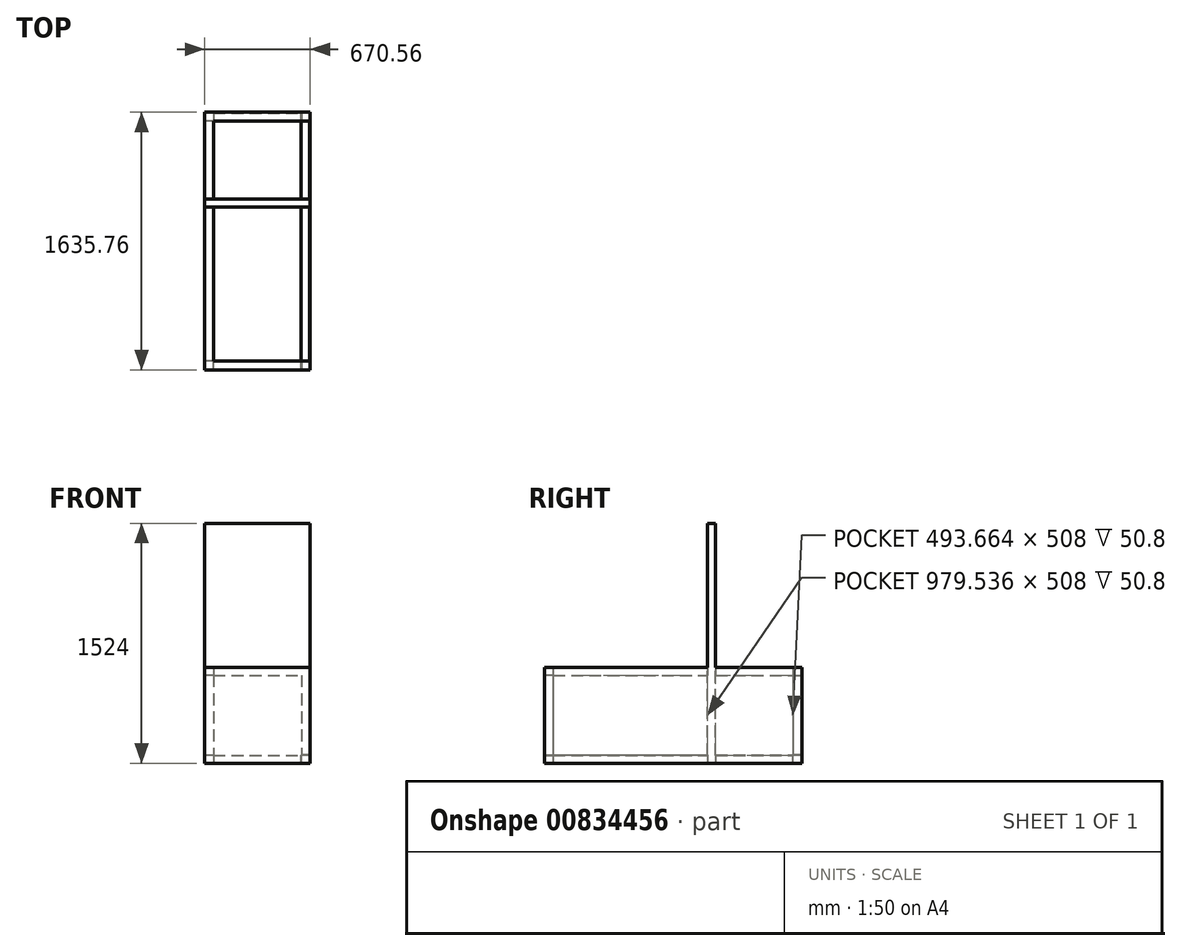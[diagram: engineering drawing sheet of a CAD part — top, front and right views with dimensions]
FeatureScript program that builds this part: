
annotation { "Feature Type Name" : "Feature", "Feature Type Description" : "" }
export const myFeature = defineFeature(function(context is Context, id is Id, definition is map)
    precondition{}
    {
        {
            var Q0;
            Q0=qCreatedBy(makeId("Top.planeOp"),FACE);
            var sketch = newSketch(context, id + "F0", { "sketchPlane" : qUnion([Q0])});
            skLineSegment(sketch, "E0.bottom", {"start": v(-609.6, -762) * mm, "end": v(609.6, -762) * mm});
            skLineSegment(sketch, "E0.top", {"start": v(-609.6, 762) * mm, "end": v(609.6, 762) * mm});
            skLineSegment(sketch, "E0.left", {"start": v(-609.6, -762) * mm, "end": v(-609.6, 762) * mm});
            skLineSegment(sketch, "E0.right", {"start": v(609.6, -762) * mm, "end": v(609.6, 762) * mm});
            skPoint(sketch, "E0.middle", {"position": v(0, 0) * mm});
            skLineSegment(sketch, "E1.0", {"start": v(660.4, -812.8) * mm, "end": v(660.4, 812.8) * mm});
            skLineSegment(sketch, "E1.1", {"start": v(-660.4, -812.8) * mm, "end": v(660.4, -812.8) * mm});
            skLineSegment(sketch, "E1.2", {"start": v(-660.4, -812.8) * mm, "end": v(-660.4, 812.8) * mm});
            skLineSegment(sketch, "E1.3", {"start": v(-660.4, 812.8) * mm, "end": v(660.4, 812.8) * mm});
            skSolve(sketch);
        }
        {
            var Q0;
            Q0=makeQuery(id+"F0.imprint","IMPRINT",FACE,{"disambiguationData":[TD([[makeQuery(id+"F0.imprint","IMPRINT",EDGE,{"derivedFrom":sQuery(id+"F0.wireOp",EDGE,"E0.bottom")}),-1.0]])]});
            extrude(context, id + "F1", {"entities" : qUnion([Q0]), "depth" : 50.8 * mm, "offsetDistance" : 25.4 * mm});
        }
        {
            var Q0;
            Q0=makeQuery(id+"F1.opExtrude","CAP_FACE",FACE,{"disambiguationData":[OSD([sQuery(id+"F0.wireOp",EDGE,"E0.bottom"),sQuery(id+"F0.wireOp",EDGE,"E0.top"),sQuery(id+"F0.wireOp",EDGE,"E0.left"),sQuery(id+"F0.wireOp",EDGE,"E0.right"),sQuery(id+"F0.wireOp",EDGE,"E1.0"),sQuery(id+"F0.wireOp",EDGE,"E1.1"),sQuery(id+"F0.wireOp",EDGE,"E1.2"),sQuery(id+"F0.wireOp",EDGE,"E1.3")])],"isStart":false});
            var sketch = newSketch(context, id + "F2", { "sketchPlane" : qUnion([Q0])});
            skLineSegment(sketch, "E2", {"start": v(-660.4, 812.8) * mm, "end": v(-609.6, 812.8) * mm});
            skLineSegment(sketch, "E3", {"start": v(-609.6, 812.8) * mm, "end": v(-609.6, 762) * mm});
            skLineSegment(sketch, "E4", {"start": v(-609.6, 762) * mm, "end": v(-660.4, 762) * mm});
            skLineSegment(sketch, "E5", {"start": v(-660.4, 762) * mm, "end": v(-660.4, 812.8) * mm});
            skLineSegment(sketch, "E6.MirrorCS", {"start": v(660.4, 812.8) * mm, "end": v(609.6, 812.8) * mm});
            skLineSegment(sketch, "E7.MirrorCS", {"start": v(609.6, 812.8) * mm, "end": v(609.6, 762) * mm});
            skLineSegment(sketch, "E8.MirrorCS", {"start": v(660.4, 762) * mm, "end": v(660.4, 812.8) * mm});
            skLineSegment(sketch, "E9.MirrorCS", {"start": v(609.6, 762) * mm, "end": v(660.4, 762) * mm});
            skLineSegment(sketch, "E10.MirrorCS", {"start": v(609.6, -762) * mm, "end": v(660.4, -762) * mm});
            skLineSegment(sketch, "E11.MirrorCS", {"start": v(-660.4, -812.8) * mm, "end": v(-609.6, -812.8) * mm});
            skLineSegment(sketch, "E12.MirrorCS", {"start": v(-609.6, -812.8) * mm, "end": v(-609.6, -762) * mm});
            skLineSegment(sketch, "E13.MirrorCS", {"start": v(660.4, -762) * mm, "end": v(660.4, -812.8) * mm});
            skLineSegment(sketch, "E14.MirrorCS", {"start": v(-609.6, -762) * mm, "end": v(-660.4, -762) * mm});
            skLineSegment(sketch, "E15.MirrorCS", {"start": v(609.6, -812.8) * mm, "end": v(609.6, -762) * mm});
            skLineSegment(sketch, "E16.MirrorCS", {"start": v(660.4, -812.8) * mm, "end": v(609.6, -812.8) * mm});
            skLineSegment(sketch, "E17.MirrorCS", {"start": v(-660.4, -762) * mm, "end": v(-660.4, -812.8) * mm});
            skSolve(sketch);
        }
        {
            var Q0;
            Q0=qSketchRegion(id+"F2",true);
            extrude(context, id + "F3", {"entities" : qUnion([Q0]), "operationType" : NewBodyOperationType.ADD, "depth" : 508 * mm, "offsetDistance" : 25.4 * mm});
        }
        {
            var Q0;
            Q0=makeQuery(id+"F3.opExtrude","CAP_FACE",FACE,{"disambiguationData":[OSD([sQuery(id+"F2.wireOp",EDGE,"E2"),sQuery(id+"F2.wireOp",EDGE,"E3"),sQuery(id+"F2.wireOp",EDGE,"E4"),sQuery(id+"F2.wireOp",EDGE,"E5")])],"isStart":false});
            var sketch = newSketch(context, id + "F4", { "sketchPlane" : qUnion([Q0])});
            skLineSegment(sketch, "E18.bottom", {"start": v(-609.6, -762) * mm, "end": v(609.6, -762) * mm});
            skLineSegment(sketch, "E18.top", {"start": v(-609.6, 762) * mm, "end": v(609.6, 762) * mm});
            skLineSegment(sketch, "E18.left", {"start": v(-609.6, -762) * mm, "end": v(-609.6, 762) * mm});
            skLineSegment(sketch, "E18.right", {"start": v(609.6, -762) * mm, "end": v(609.6, 762) * mm});
            skPoint(sketch, "E18.middle", {"position": v(0, 0) * mm});
            skLineSegment(sketch, "E19.0", {"start": v(-660.4, -812.8) * mm, "end": v(660.4, -812.8) * mm});
            skLineSegment(sketch, "E19.1", {"start": v(-660.4, -812.8) * mm, "end": v(-660.4, 812.8) * mm});
            skLineSegment(sketch, "E19.2", {"start": v(-660.4, 812.8) * mm, "end": v(660.4, 812.8) * mm});
            skLineSegment(sketch, "E19.3", {"start": v(660.4, -812.8) * mm, "end": v(660.4, 812.8) * mm});
            skSolve(sketch);
        }
        {
            var Q0;
            Q0=qSketchRegion(id+"F4",true);
            extrude(context, id + "F5", {"entities" : qUnion([Q0]), "operationType" : NewBodyOperationType.ADD, "depth" : 50.8 * mm, "offsetDistance" : 25.4 * mm});
        }
        {
            var Q0;
            Q0=makeQuery(id+"F5.opExtrude","SWEPT_FACE",FACE,{"disambiguationData":[OSD([sQuery(id+"F4.wireOp",EDGE,"E18.top")])]});
            var sketch = newSketch(context, id + "F6", { "sketchPlane" : qUnion([Q0])});
            skLineSegment(sketch, "E20", {"start": v(-609.6, 558.8) * mm, "end": v(-609.6, 609.6) * mm});
            skLineSegment(sketch, "E21", {"start": v(-609.6, 609.6) * mm, "end": v(0, 609.6) * mm});
            skLineSegment(sketch, "E22", {"start": v(0, 609.6) * mm, "end": v(0, 558.8) * mm});
            skLineSegment(sketch, "E23", {"start": v(0, 558.8) * mm, "end": v(-609.6, 558.8) * mm});
            skSolve(sketch);
        }
        {
            var Q0;
            Q0=makeQuery(id+"FCSgfiYEbyqsPuG_1.boolean.opBoolean","MERGE",FACE,{"derivedFrom":[makeQuery(id+"F5.opExtrude","CAP_FACE",FACE,{"disambiguationData":[OSD([sQuery(id+"F4.wireOp",EDGE,"E18.bottom"),sQuery(id+"F4.wireOp",EDGE,"E18.top"),sQuery(id+"F4.wireOp",EDGE,"E18.left"),sQuery(id+"F4.wireOp",EDGE,"E18.right"),sQuery(id+"F4.wireOp",EDGE,"E19.0"),sQuery(id+"F4.wireOp",EDGE,"E19.1"),sQuery(id+"F4.wireOp",EDGE,"E19.2"),sQuery(id+"F4.wireOp",EDGE,"E19.3")])],"isStart":false}),makeQuery(id+"FCSgfiYEbyqsPuG_1.opExtrude","SWEPT_FACE",FACE,{"disambiguationData":[OSD([sQuery(id+"F6.wireOp",EDGE,"E21")])]})]});
            var sketch = newSketch(context, id + "F7", { "sketchPlane" : qUnion([Q0])});
            skLineSegment(sketch, "E24", {"start": v(0, 762) * mm, "end": v(0, 812.8) * mm});
            skLineSegment(sketch, "E25", {"start": v(0, 812.8) * mm, "end": v(660.4, 812.8) * mm});
            skLineSegment(sketch, "E26", {"start": v(660.4, 812.8) * mm, "end": v(660.4, -812.8) * mm});
            skLineSegment(sketch, "E27", {"start": v(660.4, -812.8) * mm, "end": v(0, -812.8) * mm});
            skLineSegment(sketch, "E28", {"start": v(0, -812.8) * mm, "end": v(0, 762) * mm});
            skSolve(sketch);
        }
        {
            var Q0;
            Q0=qSketchRegion(id+"F7",true);
            extrude(context, id + "F8", {"entities" : qUnion([Q0]), "operationType" : NewBodyOperationType.REMOVE, "endBound" : BoundingType.THROUGH_ALL, "oppositeDirection" : true, "depth" : 25.4 * mm, "offsetDistance" : 25.4 * mm});
        }
        {
            var Q0;
            {var subQ0=sQuery(id+"F0.wireOp",EDGE,"E0.left");var subQ1=sQuery(id+"F0.wireOp",EDGE,"E1.3");var subQ2=sQuery(id+"F0.wireOp",EDGE,"E0.right");var subQ3=sQuery(id+"F0.wireOp",EDGE,"E0.top");var subQ4=makeQuery(id+"F1.opExtrude","CAP_FACE",FACE,{"disambiguationData":[OSD([sQuery(id+"F0.wireOp",EDGE,"E0.bottom"),subQ3,subQ0,subQ2,sQuery(id+"F0.wireOp",EDGE,"E1.0"),sQuery(id+"F0.wireOp",EDGE,"E1.1"),sQuery(id+"F0.wireOp",EDGE,"E1.2"),subQ1])],"isStart":false});Q0=makeQuery(id+"F3.boolean.opBoolean","SPLIT",FACE,{"disambiguationData":[TD([makeQuery(id+"F1.opExtrude","SWEPT_FACE",FACE,{"disambiguationData":[OSD([subQ1])]})])],"derivedFrom":subQ4});}
            var sketch = newSketch(context, id + "F9", { "sketchPlane" : qUnion([Q0])});
            skLineSegment(sketch, "E29", {"start": v(0, 812.8) * mm, "end": v(0, 762) * mm});
            skLineSegment(sketch, "E30", {"start": v(0, 762) * mm, "end": v(-50.8, 762) * mm});
            skLineSegment(sketch, "E31", {"start": v(-50.8, 762) * mm, "end": v(-50.8, 812.8) * mm});
            skLineSegment(sketch, "E32", {"start": v(-50.8, 812.8) * mm, "end": v(0, 812.8) * mm});
            skLineSegment(sketch, "E33.MirrorCS", {"start": v(-50.8, -812.8) * mm, "end": v(0, -812.8) * mm});
            skLineSegment(sketch, "E34.MirrorCS", {"start": v(0, -812.8) * mm, "end": v(0, -762) * mm});
            skLineSegment(sketch, "E35.MirrorCS", {"start": v(0, -762) * mm, "end": v(-50.8, -762) * mm});
            skLineSegment(sketch, "E36.MirrorCS", {"start": v(-50.8, -762) * mm, "end": v(-50.8, -812.8) * mm});
            skSolve(sketch);
        }
        {
            var Q0;
            Q0=qSketchRegion(id+"F9",true);
            extrude(context, id + "F10", {"entities" : qUnion([Q0]), "operationType" : NewBodyOperationType.ADD, "endBound" : BoundingType.UP_TO_NEXT, "depth" : 25.4 * mm, "offsetDistance" : 25.4 * mm});
        }
        {
            var Q0;
            {var subQ1=sQuery(id+"F0.wireOp",EDGE,"E0.top");var subQ7=sQuery(id+"F0.wireOp",EDGE,"E0.bottom");var subQ10=makeQuery(id+"F8.opExtrude","SWEPT_FACE",FACE,{"disambiguationData":[OSD([sQuery(id+"F7.wireOp",EDGE,"E24"),sQuery(id+"F7.wireOp",EDGE,"E28")])]});Q0=makeQuery(id+"FI0uP4kL5XJLF2I_1.boolean.opBoolean","MERGE",FACE,{"derivedFrom":[makeQuery(id+"F10.boolean.opBoolean","MERGE",FACE,{"derivedFrom":[makeQuery(id+"F8.boolean.opBoolean","MERGE",FACE,{"derivedFrom":[makeQuery(id+"FCSgfiYEbyqsPuG_1.opExtrude","SWEPT_FACE",FACE,{"disambiguationData":[OSD([sQuery(id+"F6.wireOp",EDGE,"E22")])]}),subQ10]}),makeQuery(id+"F8.boolean.opBoolean","COPY",FACE,{"disambiguationData":[TD([makeQuery(id+"F1.opExtrude","SWEPT_FACE",FACE,{"disambiguationData":[OSD([subQ7])]})])],"derivedFrom":subQ10}),makeQuery(id+"F8.boolean.opBoolean","COPY",FACE,{"disambiguationData":[TD([makeQuery(id+"F1.opExtrude","SWEPT_FACE",FACE,{"disambiguationData":[OSD([subQ1])]})])],"derivedFrom":subQ10}),makeQuery(id+"F10.opExtrude","SWEPT_FACE",FACE,{"disambiguationData":[OSD([sQuery(id+"F9.wireOp",EDGE,"E29")])]}),makeQuery(id+"F10.opExtrude","SWEPT_FACE",FACE,{"disambiguationData":[OSD([sQuery(id+"F9.wireOp",EDGE,"E34.MirrorCS")])]})]}),makeQuery(id+"FI0uP4kL5XJLF2I_1.opExtrude","SWEPT_FACE",FACE,{"disambiguationData":[OSD([sQuery(id+"FPcTlZiTrbIZ70A_1.wireOp",EDGE,"L0GQmyvb-ReXV-Bmec-5JdH-0vrgJq4hWDGI")])]})]});}
            var sketch = newSketch(context, id + "F11", { "sketchPlane" : qUnion([Q0])});
            skLineSegment(sketch, "E37", {"start": v(812.8, 0) * mm, "end": v(254, 0) * mm});
            skLineSegment(sketch, "E38", {"start": v(254, 0) * mm, "end": v(254, 254) * mm});
            skLineSegment(sketch, "E39", {"start": v(254, 254) * mm, "end": v(812.8, 254) * mm});
            skLineSegment(sketch, "E40", {"start": v(812.8, 254) * mm, "end": v(812.8, 0) * mm});
            skSolve(sketch);
        }
        {
            var Q0;
            Q0=qSketchRegion(id+"F11",true);
            extrude(context, id + "F12", {"entities" : qUnion([Q0]), "operationType" : NewBodyOperationType.ADD, "depth" : 558.8 * mm, "offsetDistance" : 25.4 * mm});
        }
        {
            var Q0;
            {var subQ0=sQuery(id+"F11.wireOp",EDGE,"E38");Q0=makeQuery(id+"Fa8mDGQ4B8yroh9_1.boolean.opBoolean","MERGE",FACE,{"derivedFrom":[makeQuery(id+"F12.opExtrude","SWEPT_FACE",FACE,{"disambiguationData":[OSD([subQ0])]}),makeQuery(id+"Fa8mDGQ4B8yroh9_1.opExtrude","SWEPT_FACE",FACE,{"disambiguationData":[OSD([subQ0])]})]});}
            var sketch = newSketch(context, id + "F13", { "sketchPlane" : qUnion([Q0])});
            skLineSegment(sketch, "E41.0", {"start": v(-0.63, 203.2) * mm, "end": v(508, 203.2) * mm});
            skLineSegment(sketch, "E41.1", {"start": v(-0.63, 50.8) * mm, "end": v(-0.63, 203.2) * mm});
            skLineSegment(sketch, "E41.2", {"start": v(508, 50.8) * mm, "end": v(-0.63, 50.8) * mm});
            skLineSegment(sketch, "E41.3", {"start": v(508, 203.2) * mm, "end": v(508, 50.8) * mm});
            skSolve(sketch);
        }
        {
            var Q0;
            Q0=makeQuery(id+"FCSgfiYEbyqsPuG_1.boolean.opBoolean","MERGE",FACE,{"derivedFrom":[makeQuery(id+"F5.opExtrude","CAP_FACE",FACE,{"disambiguationData":[OSD([sQuery(id+"F4.wireOp",EDGE,"E18.bottom"),sQuery(id+"F4.wireOp",EDGE,"E18.top"),sQuery(id+"F4.wireOp",EDGE,"E18.left"),sQuery(id+"F4.wireOp",EDGE,"E18.right"),sQuery(id+"F4.wireOp",EDGE,"E19.0"),sQuery(id+"F4.wireOp",EDGE,"E19.1"),sQuery(id+"F4.wireOp",EDGE,"E19.2"),sQuery(id+"F4.wireOp",EDGE,"E19.3")])],"isStart":false}),makeQuery(id+"FCSgfiYEbyqsPuG_1.opExtrude","SWEPT_FACE",FACE,{"disambiguationData":[OSD([sQuery(id+"F6.wireOp",EDGE,"E21")])]})]});
            var sketch = newSketch(context, id + "F14", { "sketchPlane" : qUnion([Q0])});
            skLineSegment(sketch, "E42.0", {"start": v(-635, -787.4) * mm, "end": v(-635, 787.4) * mm});
            skLineSegment(sketch, "E42.1", {"start": v(-635, -787.4) * mm, "end": v(-25.4, -787.4) * mm});
            skLineSegment(sketch, "E42.2", {"start": v(-25.4, -787.4) * mm, "end": v(-25.4, 787.4) * mm});
            skLineSegment(sketch, "E42.3", {"start": v(-635, 787.4) * mm, "end": v(-25.4, 787.4) * mm});
            skSolve(sketch);
        }
        {
            var Q0;
            Q0=makeQuery(id+"F12.boolean.opBoolean","MERGE",FACE,{"derivedFrom":[makeQuery(id+"FI0uP4kL5XJLF2I_1.boolean.opBoolean","MERGE",FACE,{"derivedFrom":[makeQuery(id+"F1.opExtrude","CAP_FACE",FACE,{"disambiguationData":[OSD([sQuery(id+"F0.wireOp",EDGE,"E0.bottom"),sQuery(id+"F0.wireOp",EDGE,"E0.top"),sQuery(id+"F0.wireOp",EDGE,"E0.left"),sQuery(id+"F0.wireOp",EDGE,"E0.right"),sQuery(id+"F0.wireOp",EDGE,"E1.0"),sQuery(id+"F0.wireOp",EDGE,"E1.1"),sQuery(id+"F0.wireOp",EDGE,"E1.2"),sQuery(id+"F0.wireOp",EDGE,"E1.3")])],"isStart":true}),makeQuery(id+"FI0uP4kL5XJLF2I_1.opExtrude","SWEPT_FACE",FACE,{"disambiguationData":[OSD([sQuery(id+"FPcTlZiTrbIZ70A_1.wireOp",EDGE,"5B50FkJB-d4VW-NrSr-TGA2-GngbR9WeU5De")])]})]}),makeQuery(id+"F12.opExtrude","SWEPT_FACE",FACE,{"disambiguationData":[OSD([sQuery(id+"F11.wireOp",EDGE,"E37")])]})]});
            var sketch = newSketch(context, id + "F15", { "sketchPlane" : qUnion([Q0])});
            skSolve(sketch);
        }
        {
            var Q0;
            {var subQ0=sQuery(id+"F11.wireOp",EDGE,"E39");Q0=makeQuery(id+"Fa8mDGQ4B8yroh9_1.boolean.opBoolean","MERGE",FACE,{"derivedFrom":[makeQuery(id+"F12.opExtrude","SWEPT_FACE",FACE,{"disambiguationData":[OSD([subQ0])]}),makeQuery(id+"Fa8mDGQ4B8yroh9_1.opExtrude","SWEPT_FACE",FACE,{"disambiguationData":[OSD([subQ0])]})]});}
            var sketch = newSketch(context, id + "F16", { "sketchPlane" : qUnion([Q0])});
            skPoint(sketch, "E43", {"position": v(279.4, 533.4) * mm});
            skCircle(sketch, "E44", {"center": v(279.4, 533.4) * mm, "radius": 228.6 * mm});
            skSolve(sketch);
        }
        {
            var Q0;
            Q0=makeQuery(id+"F12.boolean.opBoolean","MERGE",FACE,{"derivedFrom":[makeQuery(id+"F10.boolean.opBoolean","MERGE",FACE,{"derivedFrom":[makeQuery(id+"F5.boolean.opBoolean","MERGE",FACE,{"derivedFrom":[makeQuery(id+"F3.boolean.opBoolean","MERGE",FACE,{"derivedFrom":[makeQuery(id+"F1.opExtrude","SWEPT_FACE",FACE,{"disambiguationData":[OSD([sQuery(id+"F0.wireOp",EDGE,"E1.3")])]}),makeQuery(id+"F3.opExtrude","SWEPT_FACE",FACE,{"disambiguationData":[OSD([sQuery(id+"F2.wireOp",EDGE,"E2")])]}),makeQuery(id+"F3.opExtrude","SWEPT_FACE",FACE,{"disambiguationData":[OSD([sQuery(id+"F2.wireOp",EDGE,"E6.MirrorCS")])]})]}),makeQuery(id+"F5.opExtrude","SWEPT_FACE",FACE,{"disambiguationData":[OSD([sQuery(id+"F4.wireOp",EDGE,"E19.2")])]})]}),makeQuery(id+"F10.opExtrude","SWEPT_FACE",FACE,{"disambiguationData":[OSD([sQuery(id+"F9.wireOp",EDGE,"E32")])]})]}),makeQuery(id+"F12.opExtrude","SWEPT_FACE",FACE,{"disambiguationData":[OSD([sQuery(id+"F11.wireOp",EDGE,"E40")])]})]});
            var sketch = newSketch(context, id + "F17", { "sketchPlane" : qUnion([Q0])});
            skLineSegment(sketch, "E45.bottom", {"start": v(0, 254) * mm, "end": v(-558.8, 254) * mm});
            skLineSegment(sketch, "E45.top", {"start": v(0, 0) * mm, "end": v(-558.8, 0) * mm});
            skLineSegment(sketch, "E45.left", {"start": v(0, 254) * mm, "end": v(0, 0) * mm});
            skLineSegment(sketch, "E45.right", {"start": v(-558.8, 254) * mm, "end": v(-558.8, 0) * mm});
            skSolve(sketch);
        }
        {
            var Q0;
            Q0=qSketchRegion(id+"F17",true);
            extrude(context, id + "F18", {"entities" : qUnion([Q0]), "operationType" : NewBodyOperationType.REMOVE, "endBound" : BoundingType.THROUGH_ALL, "oppositeDirection" : true, "depth" : 25.4 * mm, "offsetDistance" : 25.4 * mm});
        }
        {
            var Q0;
            {var subQ1=sQuery(id+"F0.wireOp",EDGE,"E0.top");var subQ7=sQuery(id+"F0.wireOp",EDGE,"E0.bottom");var subQ10=makeQuery(id+"F8.opExtrude","SWEPT_FACE",FACE,{"disambiguationData":[OSD([sQuery(id+"F7.wireOp",EDGE,"E24"),sQuery(id+"F7.wireOp",EDGE,"E28")])]});Q0=makeQuery(id+"F18.boolean.opBoolean","MERGE",FACE,{"derivedFrom":[makeQuery(id+"F10.boolean.opBoolean","MERGE",FACE,{"derivedFrom":[makeQuery(id+"F8.boolean.opBoolean","MERGE",FACE,{"derivedFrom":[makeQuery(id+"FCSgfiYEbyqsPuG_1.opExtrude","SWEPT_FACE",FACE,{"disambiguationData":[OSD([sQuery(id+"F6.wireOp",EDGE,"E22")])]}),subQ10]}),makeQuery(id+"F8.boolean.opBoolean","COPY",FACE,{"disambiguationData":[TD([makeQuery(id+"F1.opExtrude","SWEPT_FACE",FACE,{"disambiguationData":[OSD([subQ7])]})])],"derivedFrom":subQ10}),makeQuery(id+"F8.boolean.opBoolean","COPY",FACE,{"disambiguationData":[TD([makeQuery(id+"F1.opExtrude","SWEPT_FACE",FACE,{"disambiguationData":[OSD([subQ1])]})])],"derivedFrom":subQ10}),makeQuery(id+"F10.opExtrude","SWEPT_FACE",FACE,{"disambiguationData":[OSD([sQuery(id+"F9.wireOp",EDGE,"E29")])]}),makeQuery(id+"F10.opExtrude","SWEPT_FACE",FACE,{"disambiguationData":[OSD([sQuery(id+"F9.wireOp",EDGE,"E34.MirrorCS")])]})]}),makeQuery(id+"F18.opExtrude","SWEPT_FACE",FACE,{"disambiguationData":[OSD([sQuery(id+"F17.wireOp",EDGE,"E45.left")])]})]});}
            var sketch = newSketch(context, id + "F19", { "sketchPlane" : qUnion([Q0])});
            skLineSegment(sketch, "E46.bottom", {"start": v(-812.8, 609.6) * mm, "end": v(812.8, 609.6) * mm});
            skLineSegment(sketch, "E46.top", {"start": v(-812.8, 0) * mm, "end": v(812.8, 0) * mm});
            skLineSegment(sketch, "E46.left", {"start": v(-812.8, 609.6) * mm, "end": v(-812.8, 0) * mm});
            skLineSegment(sketch, "E46.right", {"start": v(812.8, 609.6) * mm, "end": v(812.8, 0) * mm});
            skSolve(sketch);
        }
        {
            var Q0;
            Q0=qSketchRegion(id+"F19",true);
            extrude(context, id + "F20", {"entities" : qUnion([Q0]), "operationType" : NewBodyOperationType.ADD, "surfaceOperationType" : NewSurfaceOperationType.ADD, "depth" : 5.08 * mm, "offsetDistance" : 25.4 * mm});
        }
        {
            var Q0;
            Q0=makeQuery(id+"F5.boolean.opBoolean","MERGE",FACE,{"derivedFrom":[makeQuery(id+"F3.boolean.opBoolean","MERGE",FACE,{"derivedFrom":[makeQuery(id+"F1.opExtrude","SWEPT_FACE",FACE,{"disambiguationData":[OSD([sQuery(id+"F0.wireOp",EDGE,"E1.2")])]}),makeQuery(id+"F3.opExtrude","SWEPT_FACE",FACE,{"disambiguationData":[OSD([sQuery(id+"F2.wireOp",EDGE,"E5")])]}),makeQuery(id+"F3.opExtrude","SWEPT_FACE",FACE,{"disambiguationData":[OSD([sQuery(id+"F2.wireOp",EDGE,"E17.MirrorCS")])]})]}),makeQuery(id+"F5.opExtrude","SWEPT_FACE",FACE,{"disambiguationData":[OSD([sQuery(id+"F4.wireOp",EDGE,"E19.1")])]})]});
            var sketch = newSketch(context, id + "F21", { "sketchPlane" : qUnion([Q0])});
            skLineSegment(sketch, "E47.bottom", {"start": v(-812.8, 609.6) * mm, "end": v(812.8, 609.6) * mm});
            skLineSegment(sketch, "E47.top", {"start": v(-812.8, 0) * mm, "end": v(812.8, 0) * mm});
            skLineSegment(sketch, "E47.left", {"start": v(-812.8, 609.6) * mm, "end": v(-812.8, 0) * mm});
            skLineSegment(sketch, "E47.right", {"start": v(812.8, 609.6) * mm, "end": v(812.8, 0) * mm});
            skSolve(sketch);
        }
        {
            var Q0;
            Q0=qSketchRegion(id+"F21",true);
            extrude(context, id + "F22", {"entities" : qUnion([Q0]), "operationType" : NewBodyOperationType.ADD, "depth" : 5.08 * mm, "offsetDistance" : 25.4 * mm});
        }
        {
            var Q0;
            Q0=makeQuery(id+"F20.opExtrude","CAP_FACE",FACE,{"disambiguationData":[OSD([sQuery(id+"F19.wireOp",EDGE,"E46.bottom"),sQuery(id+"F19.wireOp",EDGE,"E46.top"),sQuery(id+"F19.wireOp",EDGE,"E46.left"),sQuery(id+"F19.wireOp",EDGE,"E46.right")])],"isStart":true});
            var sketch = newSketch(context, id + "F23", { "sketchPlane" : qUnion([Q0])});
            skLineSegment(sketch, "E48.bottom", {"start": v(811.74, 0) * mm, "end": v(-815.7, 0) * mm});
            skLineSegment(sketch, "E48.top", {"start": v(811.74, 51.7) * mm, "end": v(-815.7, 51.7) * mm});
            skLineSegment(sketch, "E48.left", {"start": v(811.74, 0) * mm, "end": v(811.74, 51.7) * mm});
            skLineSegment(sketch, "E48.right", {"start": v(-815.7, 0) * mm, "end": v(-815.7, 51.7) * mm});
            skSolve(sketch);
        }
        {
            var Q0;
            Q0=qSketchRegion(id+"F23",true);
            extrude(context, id + "F24", {"entities" : qUnion([Q0]), "operationType" : NewBodyOperationType.ADD, "depth" : 53.34 * mm, "offsetDistance" : 25.4 * mm});
        }
        {
            var Q0;
            Q0=makeQuery(id+"F20.opExtrude","CAP_FACE",FACE,{"disambiguationData":[OSD([sQuery(id+"F19.wireOp",EDGE,"E46.bottom"),sQuery(id+"F19.wireOp",EDGE,"E46.top"),sQuery(id+"F19.wireOp",EDGE,"E46.left"),sQuery(id+"F19.wireOp",EDGE,"E46.right")])],"isStart":false});
            var sketch = newSketch(context, id + "F25", { "sketchPlane" : qUnion([Q0])});
            skLineSegment(sketch, "E49.bottom", {"start": v(217.54, 0) * mm, "end": v(268.34, 0) * mm});
            skLineSegment(sketch, "E49.top", {"start": v(217.54, 609.6) * mm, "end": v(268.34, 609.6) * mm});
            skLineSegment(sketch, "E49.left", {"start": v(217.54, 0) * mm, "end": v(217.54, 609.6) * mm});
            skLineSegment(sketch, "E49.right", {"start": v(268.34, 0) * mm, "end": v(268.34, 609.6) * mm});
            skSolve(sketch);
        }
        {
            var Q0;
            Q0=qSketchRegion(id+"F25",true);
            var Q1;
            Q1=makeQuery(id+"F22.opExtrude","CAP_FACE",FACE,{"disambiguationData":[OSD([sQuery(id+"F21.wireOp",EDGE,"E47.bottom"),sQuery(id+"F21.wireOp",EDGE,"E47.top"),sQuery(id+"F21.wireOp",EDGE,"E47.left"),sQuery(id+"F21.wireOp",EDGE,"E47.right")])],"isStart":true});
            extrude(context, id + "F26", {"entities" : qUnion([Q0]), "operationType" : NewBodyOperationType.ADD, "depth" : 0 * mm, "offsetDistance" : 25.4 * mm, "hasSecondDirection" : true, "secondDirectionBound" : SecondDirectionBoundingType.UP_TO_SURFACE, "secondDirectionOppositeDirection" : true, "secondDirectionDepth" : 609.6 * mm, "secondDirectionBoundEntityFace" : qUnion([Q1])});
        }
        {
            var Q0;
            Q0=makeQuery(id+"F22.boolean.opBoolean","MERGE",FACE,{"derivedFrom":[makeQuery(id+"F20.boolean.opBoolean","MERGE",FACE,{"derivedFrom":[makeQuery(id+"F12.boolean.opBoolean","MERGE",FACE,{"derivedFrom":[makeQuery(id+"F10.boolean.opBoolean","MERGE",FACE,{"derivedFrom":[makeQuery(id+"F5.boolean.opBoolean","MERGE",FACE,{"derivedFrom":[makeQuery(id+"F3.boolean.opBoolean","MERGE",FACE,{"derivedFrom":[makeQuery(id+"F1.opExtrude","SWEPT_FACE",FACE,{"disambiguationData":[OSD([sQuery(id+"F0.wireOp",EDGE,"E1.3")])]}),makeQuery(id+"F3.opExtrude","SWEPT_FACE",FACE,{"disambiguationData":[OSD([sQuery(id+"F2.wireOp",EDGE,"E2")])]}),makeQuery(id+"F3.opExtrude","SWEPT_FACE",FACE,{"disambiguationData":[OSD([sQuery(id+"F2.wireOp",EDGE,"E6.MirrorCS")])]})]}),makeQuery(id+"F5.opExtrude","SWEPT_FACE",FACE,{"disambiguationData":[OSD([sQuery(id+"F4.wireOp",EDGE,"E19.2")])]})]}),makeQuery(id+"F10.opExtrude","SWEPT_FACE",FACE,{"disambiguationData":[OSD([sQuery(id+"F9.wireOp",EDGE,"E32")])]})]}),makeQuery(id+"F12.opExtrude","SWEPT_FACE",FACE,{"disambiguationData":[OSD([sQuery(id+"F11.wireOp",EDGE,"E40")])]})]}),makeQuery(id+"F20.opExtrude","SWEPT_FACE",FACE,{"disambiguationData":[OSD([sQuery(id+"F19.wireOp",EDGE,"E46.right")])]})]}),makeQuery(id+"F22.opExtrude","SWEPT_FACE",FACE,{"disambiguationData":[OSD([sQuery(id+"F21.wireOp",EDGE,"E47.left")])]})]});
            var sketch = newSketch(context, id + "F27", { "sketchPlane" : qUnion([Q0])});
            skLineSegment(sketch, "E50.bottom", {"start": v(665.48, 0) * mm, "end": v(-5.08, 0) * mm});
            skLineSegment(sketch, "E50.top", {"start": v(665.48, 609.6) * mm, "end": v(-5.08, 609.6) * mm});
            skLineSegment(sketch, "E50.left", {"start": v(665.48, 0) * mm, "end": v(665.48, 609.6) * mm});
            skLineSegment(sketch, "E50.right", {"start": v(-5.08, 0) * mm, "end": v(-5.08, 609.6) * mm});
            skSolve(sketch);
        }
        {
            var Q0;
            Q0=qSketchRegion(id+"F27",true);
            extrude(context, id + "F28", {"entities" : qUnion([Q0]), "operationType" : NewBodyOperationType.ADD, "depth" : 5.08 * mm, "offsetDistance" : 25.4 * mm});
        }
        {
            var Q0;
            Q0=makeQuery(id+"F22.boolean.opBoolean","MERGE",FACE,{"derivedFrom":[makeQuery(id+"F20.boolean.opBoolean","MERGE",FACE,{"derivedFrom":[makeQuery(id+"F10.boolean.opBoolean","MERGE",FACE,{"derivedFrom":[makeQuery(id+"F5.boolean.opBoolean","MERGE",FACE,{"derivedFrom":[makeQuery(id+"F3.boolean.opBoolean","MERGE",FACE,{"derivedFrom":[makeQuery(id+"F1.opExtrude","SWEPT_FACE",FACE,{"disambiguationData":[OSD([sQuery(id+"F0.wireOp",EDGE,"E1.1")])]}),makeQuery(id+"F3.opExtrude","SWEPT_FACE",FACE,{"disambiguationData":[OSD([sQuery(id+"F2.wireOp",EDGE,"E11.MirrorCS")])]}),makeQuery(id+"F3.opExtrude","SWEPT_FACE",FACE,{"disambiguationData":[OSD([sQuery(id+"F2.wireOp",EDGE,"E16.MirrorCS")])]})]}),makeQuery(id+"F5.opExtrude","SWEPT_FACE",FACE,{"disambiguationData":[OSD([sQuery(id+"F4.wireOp",EDGE,"E19.0")])]})]}),makeQuery(id+"F10.opExtrude","SWEPT_FACE",FACE,{"disambiguationData":[OSD([sQuery(id+"F9.wireOp",EDGE,"E33.MirrorCS")])]})]}),makeQuery(id+"F20.opExtrude","SWEPT_FACE",FACE,{"disambiguationData":[OSD([sQuery(id+"F19.wireOp",EDGE,"E46.left")])]})]}),makeQuery(id+"F22.opExtrude","SWEPT_FACE",FACE,{"disambiguationData":[OSD([sQuery(id+"F21.wireOp",EDGE,"E47.right")])]})]});
            var sketch = newSketch(context, id + "F29", { "sketchPlane" : qUnion([Q0])});
            skLineSegment(sketch, "E51.bottom", {"start": v(-665.48, 609.6) * mm, "end": v(5.08, 609.6) * mm});
            skLineSegment(sketch, "E51.top", {"start": v(-665.48, 0) * mm, "end": v(5.08, 0) * mm});
            skLineSegment(sketch, "E51.left", {"start": v(-665.48, 609.6) * mm, "end": v(-665.48, 0) * mm});
            skLineSegment(sketch, "E51.right", {"start": v(5.08, 609.6) * mm, "end": v(5.08, 0) * mm});
            skSolve(sketch);
        }
        {
            var Q0;
            Q0=qSketchRegion(id+"F29",true);
            extrude(context, id + "F30", {"entities" : qUnion([Q0]), "operationType" : NewBodyOperationType.ADD, "depth" : 5.08 * mm, "offsetDistance" : 25.4 * mm});
        }
        {
            var Q0;
            Q0=makeQuery(id+"F30.boolean.opBoolean","MERGE",FACE,{"derivedFrom":[makeQuery(id+"F28.boolean.opBoolean","MERGE",FACE,{"derivedFrom":[makeQuery(id+"F22.boolean.opBoolean","MERGE",FACE,{"derivedFrom":[makeQuery(id+"F20.boolean.opBoolean","MERGE",FACE,{"derivedFrom":[makeQuery(id+"FCSgfiYEbyqsPuG_1.boolean.opBoolean","MERGE",FACE,{"derivedFrom":[makeQuery(id+"F5.opExtrude","CAP_FACE",FACE,{"disambiguationData":[OSD([sQuery(id+"F4.wireOp",EDGE,"E18.bottom"),sQuery(id+"F4.wireOp",EDGE,"E18.top"),sQuery(id+"F4.wireOp",EDGE,"E18.left"),sQuery(id+"F4.wireOp",EDGE,"E18.right"),sQuery(id+"F4.wireOp",EDGE,"E19.0"),sQuery(id+"F4.wireOp",EDGE,"E19.1"),sQuery(id+"F4.wireOp",EDGE,"E19.2"),sQuery(id+"F4.wireOp",EDGE,"E19.3")])],"isStart":false}),makeQuery(id+"FCSgfiYEbyqsPuG_1.opExtrude","SWEPT_FACE",FACE,{"disambiguationData":[OSD([sQuery(id+"F6.wireOp",EDGE,"E21")])]})]}),makeQuery(id+"F20.opExtrude","SWEPT_FACE",FACE,{"disambiguationData":[OSD([sQuery(id+"F19.wireOp",EDGE,"E46.bottom")])]})]}),makeQuery(id+"F22.opExtrude","SWEPT_FACE",FACE,{"disambiguationData":[OSD([sQuery(id+"F21.wireOp",EDGE,"E47.bottom")])]})]}),makeQuery(id+"F28.opExtrude","SWEPT_FACE",FACE,{"disambiguationData":[OSD([sQuery(id+"F27.wireOp",EDGE,"E50.top")])]})]}),makeQuery(id+"F30.opExtrude","SWEPT_FACE",FACE,{"disambiguationData":[OSD([sQuery(id+"F29.wireOp",EDGE,"E51.bottom")])]})]});
            var sketch = newSketch(context, id + "F31", { "sketchPlane" : qUnion([Q0])});
            skLineSegment(sketch, "E52.bottom", {"start": v(5.08, 217.53) * mm, "end": v(-665.48, 217.53) * mm});
            skLineSegment(sketch, "E52.top", {"start": v(5.08, 268.33) * mm, "end": v(-665.48, 268.33) * mm});
            skLineSegment(sketch, "E52.left", {"start": v(5.08, 217.53) * mm, "end": v(5.08, 268.33) * mm});
            skLineSegment(sketch, "E52.right", {"start": v(-665.48, 217.53) * mm, "end": v(-665.48, 268.33) * mm});
            skSolve(sketch);
        }
        {
            var Q0;
            Q0 = qSketchRegion(id + "F31", true);
            extrude(context, id + "F32", {"entities" : qUnion([Q0]), "operationType" : NewBodyOperationType.ADD, "depth" : 914.4 * mm, "offsetDistance" : 25.4 * mm});
        }
    });
